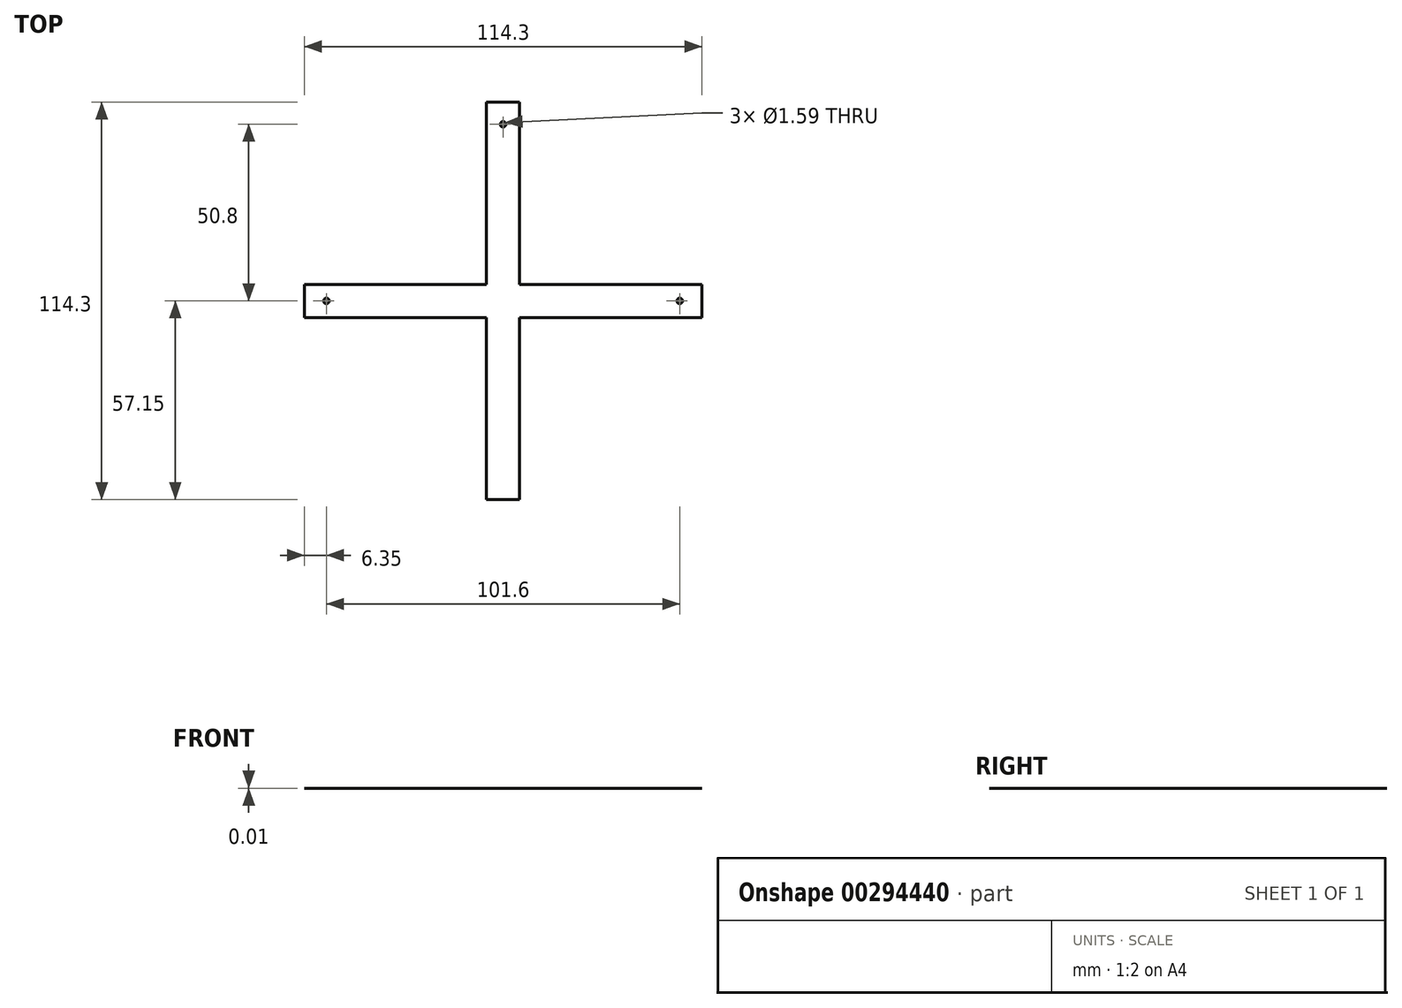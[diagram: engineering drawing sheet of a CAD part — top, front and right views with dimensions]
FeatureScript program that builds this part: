
annotation { "Feature Type Name" : "Feature", "Feature Type Description" : "" }
export const myFeature = defineFeature(function(context is Context, id is Id, definition is map)
    precondition{}
    {
        {
            var Q0;
            Q0=qCreatedBy(makeId("Top.planeOp"),FACE);
            var sketch = newSketch(context, id + "F0", { "sketchPlane" : qUnion([Q0])});
            skLineSegment(sketch, "E0.bottom", {"start": v(57.15, 4.76) * mm, "end": v(-57.15, 4.76) * mm});
            skLineSegment(sketch, "E0.top", {"start": v(57.15, -4.76) * mm, "end": v(-57.15, -4.76) * mm});
            skLineSegment(sketch, "E0.left", {"start": v(57.15, 4.76) * mm, "end": v(57.15, -4.76) * mm});
            skLineSegment(sketch, "E0.right", {"start": v(-57.15, 4.76) * mm, "end": v(-57.15, -4.76) * mm});
            skPoint(sketch, "E0.middle", {"position": v(0, 0) * mm});
            skLineSegment(sketch, "E1.bottom", {"start": v(4.76, 57.15) * mm, "end": v(-4.76, 57.15) * mm});
            skLineSegment(sketch, "E1.top", {"start": v(4.76, -57.15) * mm, "end": v(-4.76, -57.15) * mm});
            skLineSegment(sketch, "E1.left", {"start": v(4.76, 57.15) * mm, "end": v(4.76, -57.15) * mm});
            skLineSegment(sketch, "E1.right", {"start": v(-4.76, 57.15) * mm, "end": v(-4.76, -57.15) * mm});
            skSolve(sketch);
        }
        {
            var Q0;
            {var subQ5=sQuery(id+"F0.wireOp",EDGE,"E1.bottom");Q0=makeQuery(id+"F0.imprint","IMPRINT",FACE,{"disambiguationData":[TD([[makeQuery(id+"F0.imprint","IMPRINT",EDGE,{"derivedFrom":subQ5}),1.0]])]});}
            var Q1;
            {var subQ0=sQuery(id+"F0.wireOp",EDGE,"E0.left");Q1=makeQuery(id+"F0.imprint","IMPRINT",FACE,{"disambiguationData":[TD([[makeQuery(id+"F0.imprint","IMPRINT",EDGE,{"derivedFrom":subQ0}),-1.0]])]});}
            var Q2;
            {var subQ0=sQuery(id+"F0.wireOp",EDGE,"E1.left");var subQ1=sQuery(id+"F0.wireOp",EDGE,"E0.bottom");var subQ2=makeQuery(id+"F0.imprint","INTERSECT",VERTEX,{"derivedFrom":[subQ1,subQ0]});Q2=makeQuery(id+"F0.imprint","IMPRINT",FACE,{"disambiguationData":[TD([[makeQuery(id+"F0.imprint","IMPRINT",EDGE,{"disambiguationData":[TD([[subQ2,-1.0]])],"derivedFrom":subQ1}),1.0]])]});}
            var Q3;
            {var subQ5=sQuery(id+"F0.wireOp",EDGE,"E1.top");Q3=makeQuery(id+"F0.imprint","IMPRINT",FACE,{"disambiguationData":[TD([[makeQuery(id+"F0.imprint","IMPRINT",EDGE,{"derivedFrom":subQ5}),-1.0]])]});}
            var Q4;
            {var subQ0=sQuery(id+"F0.wireOp",EDGE,"E0.right");Q4=makeQuery(id+"F0.imprint","IMPRINT",FACE,{"disambiguationData":[TD([[makeQuery(id+"F0.imprint","IMPRINT",EDGE,{"derivedFrom":subQ0}),1.0]])]});}
            extrude(context, id + "F1", {"entities" : qUnion([Q0, Q1, Q2, Q3, Q4]), "depth" : 3 / 203.2 * mm});
        }
        {
            var Q0;
            Q0=makeQuery(id+"F1.opExtrude","CAP_FACE",FACE,{"disambiguationData":[OSD([sQuery(id+"F0.wireOp",EDGE,"E0.bottom"),sQuery(id+"F0.wireOp",EDGE,"E0.top"),sQuery(id+"F0.wireOp",EDGE,"E0.left"),sQuery(id+"F0.wireOp",EDGE,"E0.right"),sQuery(id+"F0.wireOp",EDGE,"E1.bottom"),sQuery(id+"F0.wireOp",EDGE,"E1.top"),sQuery(id+"F0.wireOp",EDGE,"E1.left"),sQuery(id+"F0.wireOp",EDGE,"E1.right")])],"isStart":false});
            var sketch = newSketch(context, id + "F2", { "sketchPlane" : qUnion([Q0])});
            skCircle(sketch, "E2", {"center": v(0, 50.8) * mm, "radius": 0.8 * mm});
            skCircle(sketch, "E3", {"center": v(50.8, 0) * mm, "radius": 0.8 * mm});
            skCircle(sketch, "E4", {"center": v(-50.8, 0) * mm, "radius": 0.8 * mm});
            skSolve(sketch);
        }
        {
            var Q0;
            Q0 = qSketchRegion(id + "F2", true);
            extrude(context, id + "F3", {"entities" : qUnion([Q0]), "operationType" : NewBodyOperationType.REMOVE, "oppositeDirection" : true, "depth" : 9.52 * mm});
        }
        {
            var Q0;
            {var subQ0=sQuery(id+"F0.wireOp",EDGE,"E1.right");Q0=makeQuery(id+"F1.opExtrude","SWEPT_FACE",FACE,{"disambiguationData":[OSD([subQ0]),TDD([makeQuery(id+"F0.imprint","IMPRINT",EDGE,{"disambiguationData":[TD([[makeQuery(id+"F0.imprint","INTERSECT",VERTEX,{"derivedFrom":[sQuery(id+"F0.wireOp",EDGE,"E1.top"),subQ0]}),1.0]])],"derivedFrom":subQ0})])]});}
            var sketch = newSketch(context, id + "F4", { "sketchPlane" : qUnion([Q0])});
            skCircle(sketch, "E5", {"center": v(50.8, 4.76) * mm, "radius": 0.8 * mm});
            skSolve(sketch);
        }
        {
            var Q0;
            Q0=makeQuery(id+"F4.imprint","IMPRINT",FACE,{"disambiguationData":[TD([[makeQuery(id+"F4.imprint","IMPRINT",EDGE,{"derivedFrom":sQuery(id+"F4.wireOp",EDGE,"E5")}),1.0]])]});
            extrude(context, id + "F5", {"entities" : qUnion([Q0]), "operationType" : NewBodyOperationType.REMOVE, "oppositeDirection" : true, "depth" : 3 / 203.2 * mm});
        }
        {
            var Q0;
            Q0=qCreatedBy(makeId("Top.planeOp"),FACE);
            var sketch = newSketch(context, id + "F6", { "sketchPlane" : qUnion([Q0])});
            skLineSegment(sketch, "E6.bottom", {"start": v(32.2, 11.3) * mm, "end": v(-32.2, 11.3) * mm});
            skLineSegment(sketch, "E6.top", {"start": v(32.2, -9.7) * mm, "end": v(-32.2, -9.7) * mm});
            skLineSegment(sketch, "E6.left", {"start": v(32.2, 11.3) * mm, "end": v(32.2, -9.7) * mm});
            skLineSegment(sketch, "E6.right", {"start": v(-32.2, 11.3) * mm, "end": v(-32.2, -9.7) * mm});
            skPoint(sketch, "E6.middle", {"position": v(0, 0) * mm});
            skSolve(sketch);
        }
        {
            var Q0;
            Q0 = qSketchRegion(id + "F6", true);
            extrude(context, id + "F7", {"entities" : qUnion([Q0]), "endBound" : BoundingType.SYMMETRIC, "depth" : 22.3 * mm});
        }
        {
            var Q0;
            Q0=makeQuery(id+"F7.opExtrude","SWEPT_BODY",BODY,{"disambiguationData":[OSD([sQuery(id+"F6.wireOp",EDGE,"E6.bottom"),sQuery(id+"F6.wireOp",EDGE,"E6.top"),sQuery(id+"F6.wireOp",EDGE,"E6.left"),sQuery(id+"F6.wireOp",EDGE,"E6.right")])]});
            deleteBodies(context, id + "F8", {"entities" : qUnion([Q0])});
        }
    });
